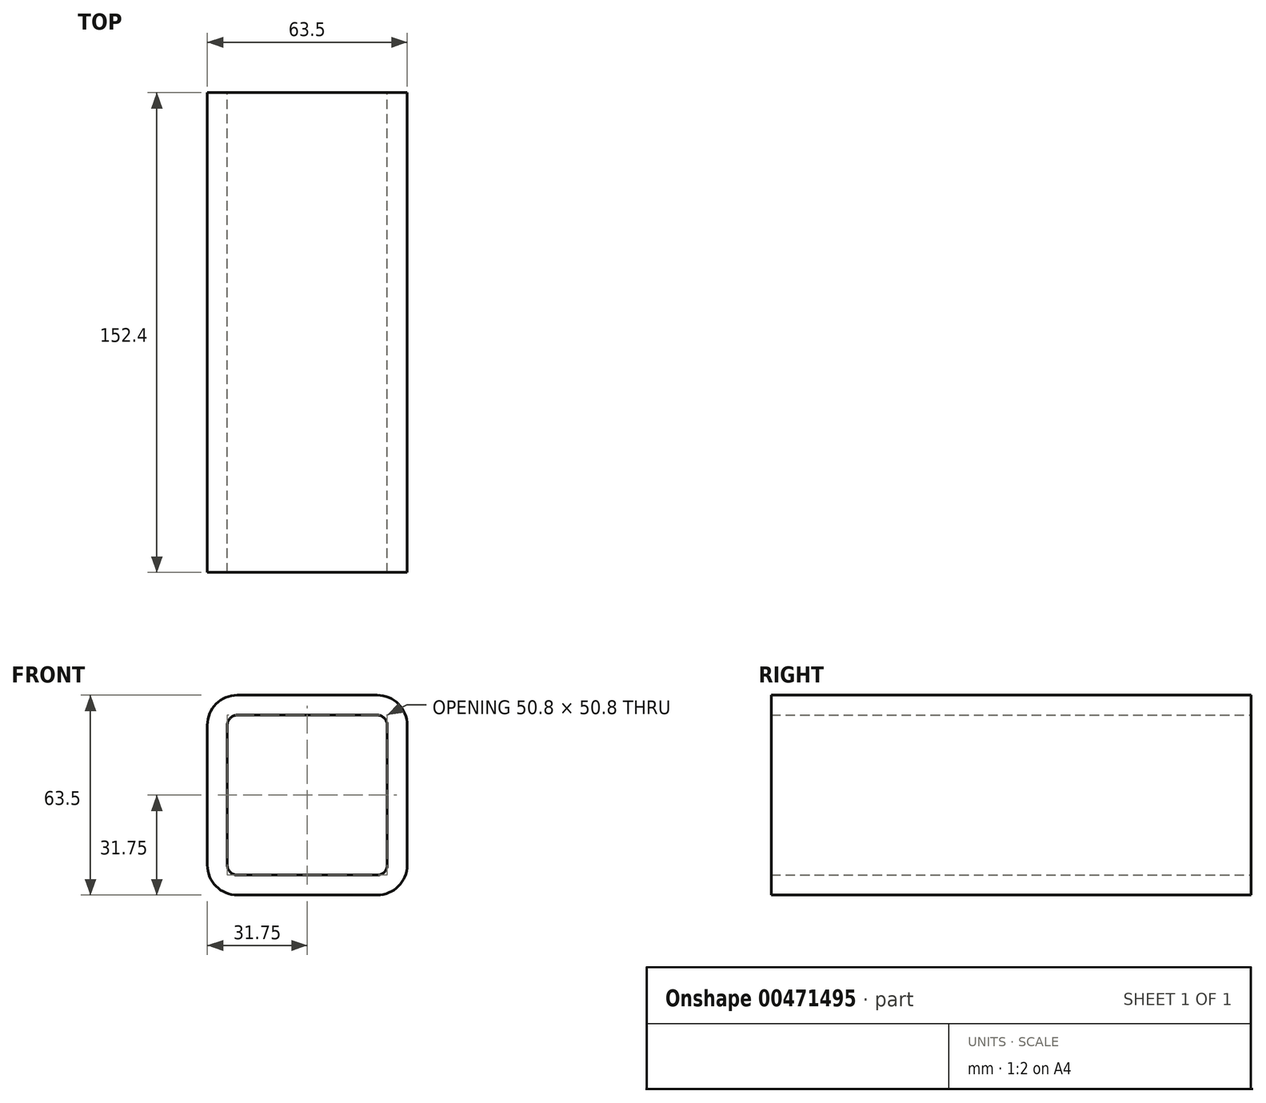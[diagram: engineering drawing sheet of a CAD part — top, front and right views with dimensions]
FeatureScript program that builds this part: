
annotation { "Feature Type Name" : "Feature", "Feature Type Description" : "" }
export const myFeature = defineFeature(function(context is Context, id is Id, definition is map)
    precondition{}
    {
        {
            var Q0;
            Q0=qCreatedBy(makeId("Front.planeOp"),FACE);
            var sketch = newSketch(context, id + "F0", { "sketchPlane" : qUnion([Q0])});
            skLineSegment(sketch, "E0.bottom", {"start": v(9.52, 0) * mm, "end": v(53.97, 0) * mm});
            skLineSegment(sketch, "E0.top", {"start": v(9.52, 63.5) * mm, "end": v(53.97, 63.5) * mm});
            skLineSegment(sketch, "E0.left", {"start": v(0, 9.52) * mm, "end": v(0, 53.98) * mm});
            skLineSegment(sketch, "E0.right", {"start": v(63.5, 9.53) * mm, "end": v(63.5, 53.98) * mm});
            skPoint(sketch, "E1.visualSharp", {"position": v(0, 63.5) * mm});
            skArc(sketch, "E1.filletArc", {"start": v(9.52, 63.5) * mm, "mid": v(2.79, 60.71) * mm, "end": v(0, 53.98) * mm});
            skPoint(sketch, "E2.visualSharp", {"position": v(63.5, 63.5) * mm});
            skArc(sketch, "E2.filletArc", {"start": v(63.5, 53.98) * mm, "mid": v(60.71, 60.71) * mm, "end": v(53.97, 63.5) * mm});
            skPoint(sketch, "E3.visualSharp", {"position": v(63.5, 0) * mm});
            skArc(sketch, "E3.filletArc", {"start": v(53.97, 0) * mm, "mid": v(60.71, 2.79) * mm, "end": v(63.5, 9.53) * mm});
            skPoint(sketch, "E4.visualSharp", {"position": v(0, 0) * mm});
            skArc(sketch, "E4.filletArc", {"start": v(0, 9.52) * mm, "mid": v(2.79, 2.79) * mm, "end": v(9.52, 0) * mm});
            skSolve(sketch);
        }
        {
            var Q0;
            Q0=makeQuery(id+"F0.imprint","IMPRINT",FACE,{"disambiguationData":[TD([[makeQuery(id+"F0.imprint","IMPRINT",EDGE,{"derivedFrom":sQuery(id+"F0.wireOp",EDGE,"E0.bottom")}),1.0]])]});
            extrude(context, id + "F1", {"entities" : qUnion([Q0]), "depth" : 152.4 * mm, "offsetDistance" : 25.4 * mm});
        }
        {
            var Q0;
            Q0=makeQuery(id+"F1.opExtrude","CAP_FACE",FACE,{"disambiguationData":[OSD([sQuery(id+"F0.wireOp",EDGE,"E0.bottom"),sQuery(id+"F0.wireOp",EDGE,"E0.top"),sQuery(id+"F0.wireOp",EDGE,"E0.left"),sQuery(id+"F0.wireOp",EDGE,"E0.right"),sQuery(id+"F0.wireOp",EDGE,"E1.filletArc"),sQuery(id+"F0.wireOp",EDGE,"E2.filletArc"),sQuery(id+"F0.wireOp",EDGE,"E3.filletArc"),sQuery(id+"F0.wireOp",EDGE,"E4.filletArc")])],"isStart":false});
            var Q1;
            Q1=makeQuery(id+"F1.opExtrude","CAP_FACE",FACE,{"disambiguationData":[OSD([sQuery(id+"F0.wireOp",EDGE,"E0.bottom"),sQuery(id+"F0.wireOp",EDGE,"E0.top"),sQuery(id+"F0.wireOp",EDGE,"E0.left"),sQuery(id+"F0.wireOp",EDGE,"E0.right"),sQuery(id+"F0.wireOp",EDGE,"E1.filletArc"),sQuery(id+"F0.wireOp",EDGE,"E2.filletArc"),sQuery(id+"F0.wireOp",EDGE,"E3.filletArc"),sQuery(id+"F0.wireOp",EDGE,"E4.filletArc")])],"isStart":true});
            shell(context, id + "F2", {"entities" : qUnion([Q0, Q1]), "thickness" : 6.35 * mm});
        }
    });
